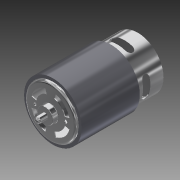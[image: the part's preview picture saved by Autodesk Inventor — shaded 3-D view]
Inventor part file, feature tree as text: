
AUTODESK INVENTOR PART (.ipt)
format: ipt  version: 2018 (Build 220112000, 112)  size: 373,248 bytes
history: native  units: mm (DEFAULTED — no unit token found)
features: sketch x15, extrude x13, fillet x3, pattern_circular x3, plane x3, hole x2, mirror x2, shell x1, chamfer x1
ambient origin geometry x8: Origin, YZ Plane, XZ Plane, XY Plane, X Axis, Y Axis, Z Axis, Center Point
bodies: Solid1 (feature_tree)
feature tree (43):
  extrude  "Extrusion1"  Depth=71.3mm TaperAngle=0.0deg
  fillet  "Fillet1"  Radius=2.0mm
  shell  "Shell1"  Thickness=0.62mm
  extrude  "Extrusion2"  Depth=4.5mm TaperAngle=0.0deg
  fillet  "Fillet2"  Radius=0.5mm
  extrude  "Extrusion3"  Depth=7.6mm TaperAngle=0.0deg
  fillet  "Fillet3"  Radius=2.5mm
  hole  "Hole1"  [1 undecoded]
  mirror  "Mirror1"
  extrude  "Extrusion4"  Depth=16.0mm
  pattern_circular  "Circular Pattern1"  Count=4 Angle=360.0deg
  plane  "Work Plane1"
  extrude  "Extrusion5"  Depth=0.62mm TaperAngle=0.0deg
  extrude  "Extrusion6"  Depth=0.62mm TaperAngle=0.0deg
  extrude  "Extrusion7"  Depth=3.0mm TaperAngle=0.0deg
  extrude  "Extrusion8"  Depth=0.8mm TaperAngle=0.0deg
  extrude  "Extrusion9"  Depth=1.0mm TaperAngle=0.0deg
  extrude  "Extrusion10"  Depth=3.15mm
  pattern_circular  "Circular Pattern2"  [2 undecoded]
  extrude  "Extrusion11"  Depth=5.9mm TaperAngle=0.0deg
  chamfer  "Chamfer1"  Distance=40.0mm Angle=360.0deg
  hole  "Hole2"  [1 undecoded]
  mirror  "Mirror2"
  plane  "Work Plane2"
  extrude  "Extrusion12"  Depth=5.9mm
  plane  "Work Plane3"
  extrude  "Flux Ring"  Depth=5.9mm
  pattern_circular  "Circular Pattern3"  [2 undecoded]
  sketch  "Sketch1"  dims[d0=42.1mm d1=71.3mm d2=0.0mm d3=2.0mm d4=0.62mm]
  sketch  "Sketch2"  dims[d5=13.0mm d6=4.5mm d7=0.0mm d8=0.5mm]
  sketch  "Sketch3"  dims[d9=5.0mm d10=7.6mm d11=0.0mm d12=2.5mm]
  sketch  "Sketch4"  dims[d13=12.5mm]
  sketch  "Sketch5"  dims[d14=2.5mm d15=6.0mm d16=4.0mm d17=2.0mm d18=14.3117mm d19=8.0mm d20=20.594885mm d21=15.0deg]
  sketch  "Sketch6"  dims[d22=15.0deg d23=16.0mm]
  sketch  "Sketch7"  dims[d24=12.0mm]
  sketch  "Sketch8"  dims[d25=10.0mm d26=0.0mm d27=40.0mm d29=360.0deg]
  sketch  "Sketch9"  dims[d30=-1.75mm d31=0.62mm d32=0.0mm]
  sketch  "Sketch10"  dims[d33=24.0mm d34=0.62mm d35=0.0mm]
  sketch  "Sketch11"  dims[d36=10.75mm d37=3.0mm d38=0.0mm]
  sketch  "Sketch12"  dims[d39=6.9mm d40=0.8mm d41=0.0mm]
  sketch  "Sketch13"  dims[d42=3.2mm d43=1.0mm d44=0.0mm]
  sketch  "Sketch14"  dims[d45=3.15mm d46=3.15mm]
  sketch  "Sketch15"  dims[d47=9.875mm d48=6.5mm d49=1.0mm d50=0.0mm d51=40.0mm d53=360.0deg d54=0.5mm d55=3.8mm d56=14.0mm d57=7.2mm d58=0.0mm d59=1.0mm d60=2.0mm d61=3.0mm d62=2.0mm d63=6.0mm d64=4.0mm d65=2.0mm d66=14.3117mm d67=1.0mm d68=20.594885mm d69=18.0mm d70=10.75mm d71=5.9mm d72=12.0mm d73=7.2mm d74=0.0mm d75=45.0deg d76=2.45mm d77=47.5mm d78=0.0mm d79=40.0mm d80=360.0deg]
note: 6 required parameter values undecoded (feature->parameter linkage not recoverable at this tier; creation-order binding heuristic only, values carry confidence <= 0.55)
